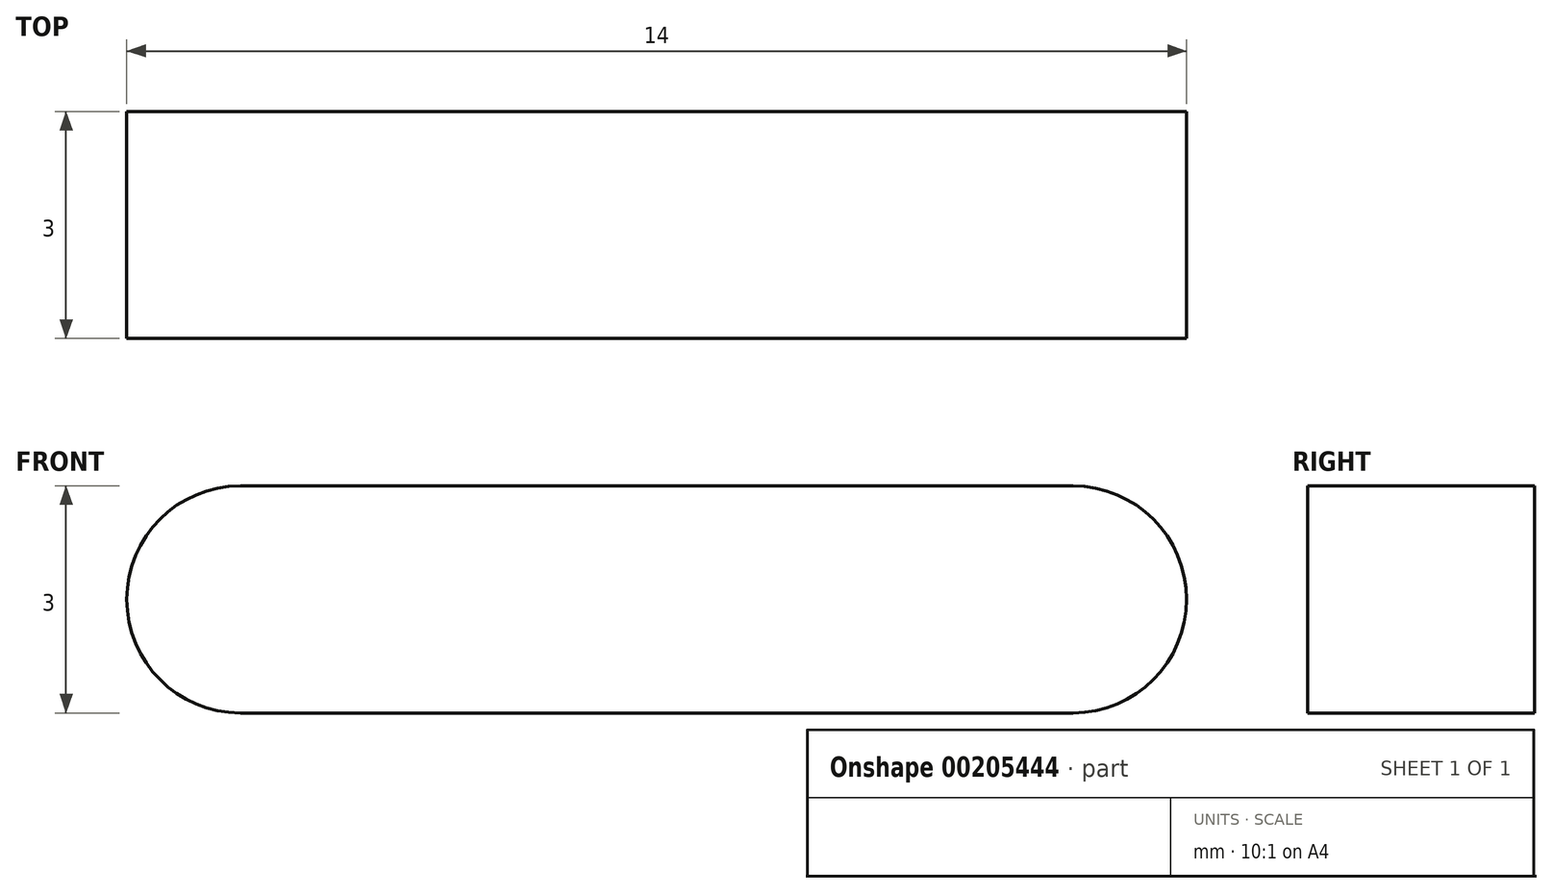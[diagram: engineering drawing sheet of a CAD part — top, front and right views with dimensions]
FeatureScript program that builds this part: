
annotation { "Feature Type Name" : "Feature", "Feature Type Description" : "" }
export const myFeature = defineFeature(function(context is Context, id is Id, definition is map)
    precondition{}
    {
        {
            var Q0;
            Q0=qCreatedBy(makeId("Front.planeOp"),FACE);
            var sketch = newSketch(context, id + "F0", { "sketchPlane" : qUnion([Q0])});
            skLineSegment(sketch, "E0.bottom", {"start": v(5.5, 1.5) * mm, "end": v(-5.5, 1.5) * mm});
            skLineSegment(sketch, "E0.top", {"start": v(5.5, -1.5) * mm, "end": v(-5.5, -1.5) * mm});
            skPoint(sketch, "E0.middle", {"position": v(0, 0) * mm});
            skArc(sketch, "E1", {"start": v(5.5, 1.5) * mm, "mid": v(7, 0) * mm, "end": v(5.5, -1.5) * mm});
            skArc(sketch, "E2", {"start": v(-5.5, 1.5) * mm, "mid": v(-7, 0) * mm, "end": v(-5.5, -1.5) * mm});
            skSolve(sketch);
        }
        {
            var Q0;
            Q0=makeQuery(id+"F0.imprint","IMPRINT",FACE,{"disambiguationData":[TD([[makeQuery(id+"F0.imprint","IMPRINT",EDGE,{"derivedFrom":sQuery(id+"F0.wireOp",EDGE,"E0.bottom")}),1.0]])]});
            extrude(context, id + "F1", {"entities" : qUnion([Q0]), "depth" : 3 * mm, "symmetric" : true});
        }
    });
